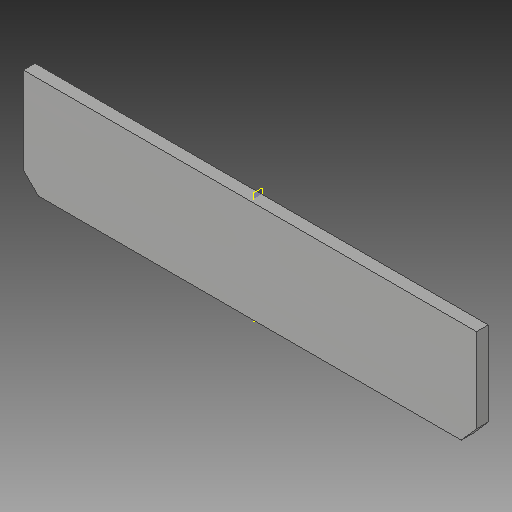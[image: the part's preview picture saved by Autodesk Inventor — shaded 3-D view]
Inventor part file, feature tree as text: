
AUTODESK INVENTOR PART (.ipt)
format: ipt  version: 2018 (Build 220112000, 112)  size: 136,192 bytes
history: native  units: mm
features: other x6, plane x1, sheet_metal_op x1, sketch x1, reference x1
ambient origin geometry x8: Origin, YZ Plane, XZ Plane, XY Plane, X Axis, Y Axis, Z Axis, Center Point
bodies: Solid1 (feature_tree)
feature tree (10):
  plane  "Work Plane1"
  sheet_metal_op  "Face1"
  other  "midtplan"
  sketch  "Sketch1"  dims[d3=45.0deg d4=7.171149mm d5=30.0mm d6=2.0mm d7=3.0mm]
  reference  "Reference1"
  other  "Plate1"
  parser-record x1  (decoder bookkeeping rows leaked as tree rows — omitted from the tree; the rows remain in map.json)
  other  "modul.iam"
  other  "plade:1"
  other  "Definition1"
note: 1 file-system path scrubbed to <path> (originals preserved in map.json)
